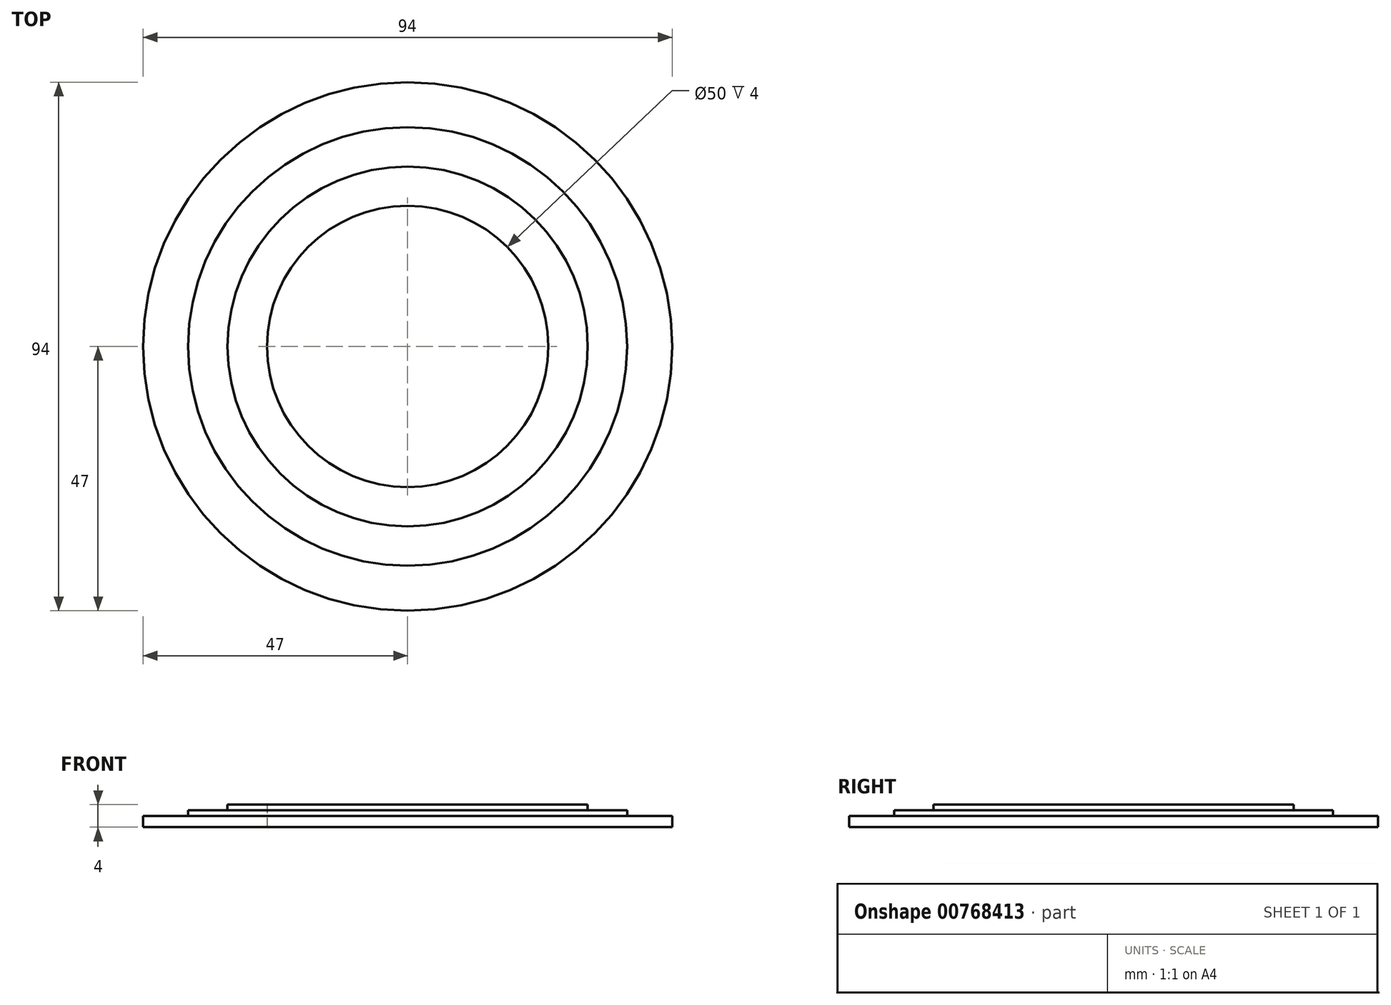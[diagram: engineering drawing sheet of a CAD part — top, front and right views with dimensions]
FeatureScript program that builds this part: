
annotation { "Feature Type Name" : "Feature", "Feature Type Description" : "" }
export const myFeature = defineFeature(function(context is Context, id is Id, definition is map)
    precondition{}
    {
        {
            var Q0;
            Q0=qCreatedBy(makeId("Front.planeOp"),FACE);
            var sketch = newSketch(context, id + "F0", { "sketchPlane" : qUnion([Q0])});
            skLineSegment(sketch, "E0", {"start": v(-25, 0) * mm, "end": v(-47, 0) * mm});
            skLineSegment(sketch, "E1", {"start": v(-47, 0) * mm, "end": v(-47, 2) * mm});
            skLineSegment(sketch, "E2", {"start": v(-32, 4) * mm, "end": v(-25, 4) * mm});
            skLineSegment(sketch, "E3", {"start": v(-25, 4) * mm, "end": v(-25, 0) * mm});
            skLineSegment(sketch, "E4", {"start": v(0, 0) * mm, "end": v(0, 4) * mm});
            skLineSegment(sketch, "E5", {"start": v(-25, 4) * mm, "end": v(-32, 4) * mm});
            skLineSegment(sketch, "E6", {"start": v(-32, 4) * mm, "end": v(-32, 3) * mm});
            skLineSegment(sketch, "E7", {"start": v(-32, 3) * mm, "end": v(-39, 3) * mm});
            skLineSegment(sketch, "E8", {"start": v(-39, 3) * mm, "end": v(-39, 2) * mm});
            skLineSegment(sketch, "E9", {"start": v(-39, 2) * mm, "end": v(-47, 2) * mm});
            skPoint(sketch, "E10.orphan", {"position": v(-47, 4) * mm});
            skSolve(sketch);
        }
        {
            var Q0;
            Q0 = qSketchRegion(id + "F0", true);
            var Q1;
            Q1=sQuery(id+"F0.wireOp",EDGE,"E4");
            revolve(context, id + "F1", {"surfaceOperationType" : NewSurfaceOperationType.NEW, "entities" : qUnion([Q0]), "axis" : qUnion([Q1]), "revolveType" : RevolveType.FULL});
        }
    });
